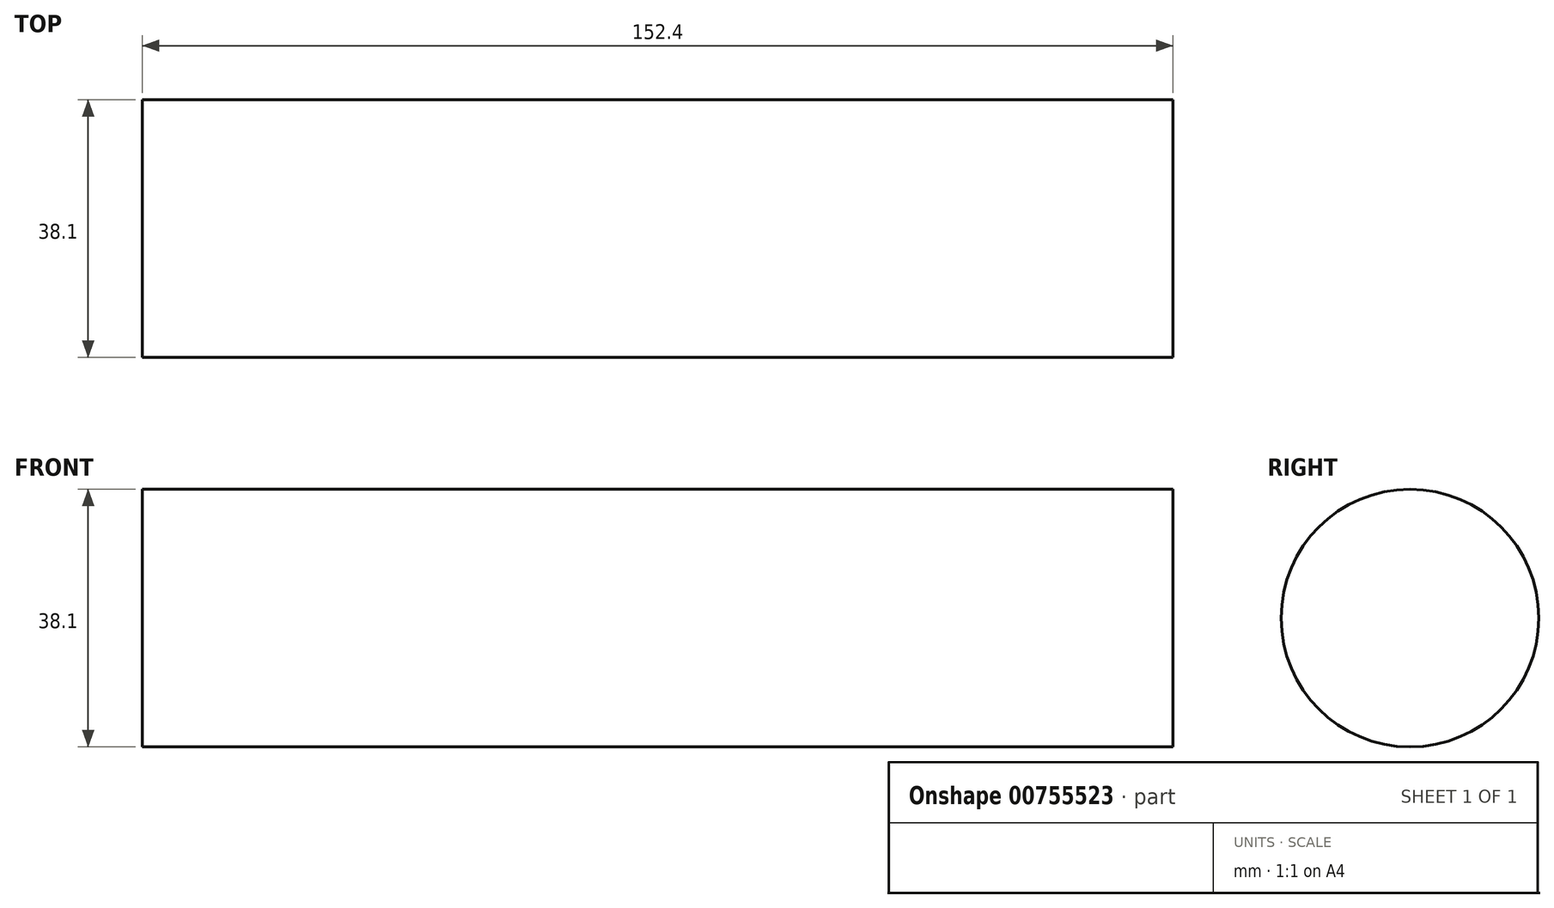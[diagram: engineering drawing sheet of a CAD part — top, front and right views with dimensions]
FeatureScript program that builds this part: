
annotation { "Feature Type Name" : "Feature", "Feature Type Description" : "" }
export const myFeature = defineFeature(function(context is Context, id is Id, definition is map)
    precondition{}
    {
        {
            var Q0;
            Q0=qCreatedBy(makeId("Right.planeOp"),FACE);
            var sketch = newSketch(context, id + "F0", { "sketchPlane" : qUnion([Q0])});
            skCircle(sketch, "E0", {"center": v(0, 0) * mm, "radius": 19.05 * mm});
            skSolve(sketch);
        }
        {
            var Q0;
            Q0 = qSketchRegion(id + "F0", true);
            extrude(context, id + "F1", {"entities" : qUnion([Q0]), "depth" : 152.4 * mm, "offsetDistance" : 25.4 * mm});
        }
    });
